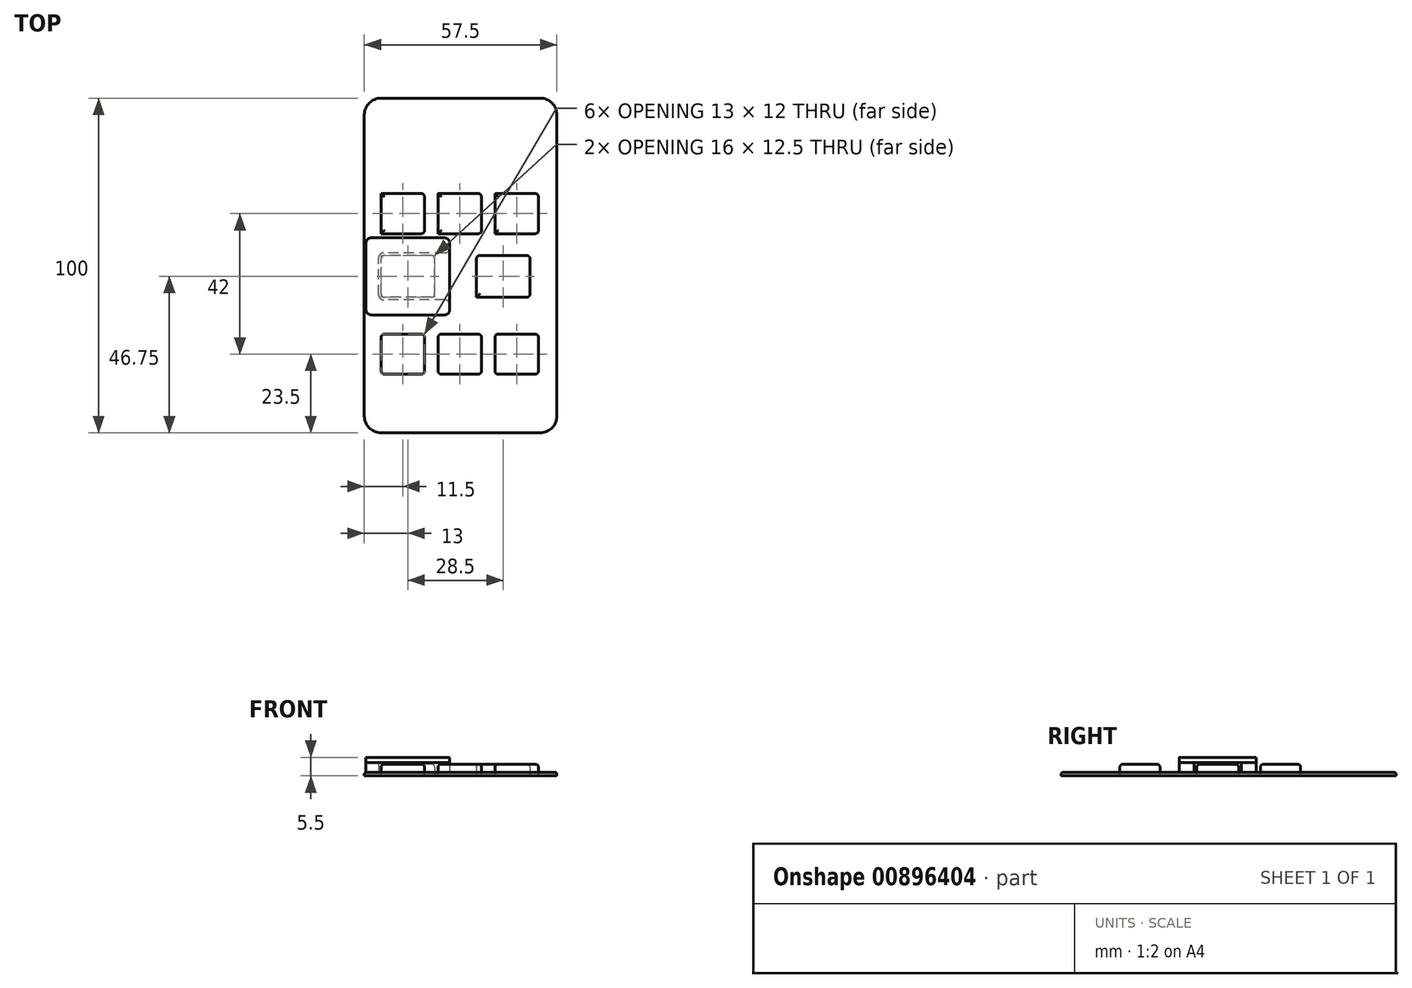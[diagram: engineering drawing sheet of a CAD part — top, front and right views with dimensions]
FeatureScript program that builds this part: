
annotation { "Feature Type Name" : "Feature", "Feature Type Description" : "" }
export const myFeature = defineFeature(function(context is Context, id is Id, definition is map)
    precondition{}
    {
        {
            var Q0;
            Q0=qCreatedBy(makeId("Top.planeOp"),FACE);
            var sketch = newSketch(context, id + "F0", { "sketchPlane" : qUnion([Q0])});
            skLineSegment(sketch, "E0.bottom", {"start": v(28.75, -50) * mm, "end": v(-28.75, -50) * mm});
            skLineSegment(sketch, "E0.top", {"start": v(28.75, 50) * mm, "end": v(-28.75, 50) * mm});
            skLineSegment(sketch, "E0.left", {"start": v(28.75, -50) * mm, "end": v(28.75, 50) * mm});
            skLineSegment(sketch, "E0.right", {"start": v(-28.75, -50) * mm, "end": v(-28.75, 50) * mm});
            skPoint(sketch, "E0.middle", {"position": v(0, 0) * mm});
            skSolve(sketch);
        }
        {
            var Q0;
            Q0=makeQuery(id+"F0.imprint","IMPRINT",FACE,{"disambiguationData":[TD([[makeQuery(id+"F0.imprint","IMPRINT",EDGE,{"derivedFrom":sQuery(id+"F0.wireOp",EDGE,"E0.bottom")}),-1.0]])]});
            extrude(context, id + "F1", {"entities" : qUnion([Q0]), "depth" : 1 * mm, "offsetDistance" : 25 * mm});
        }
        {
            var Q0;
            Q0=makeQuery(id+"F1.opExtrude","CAP_FACE",FACE,{"disambiguationData":[OSD([sQuery(id+"F0.wireOp",EDGE,"E0.bottom"),sQuery(id+"F0.wireOp",EDGE,"E0.top"),sQuery(id+"F0.wireOp",EDGE,"E0.left"),sQuery(id+"F0.wireOp",EDGE,"E0.right")])],"isStart":false});
            var sketch = newSketch(context, id + "F2", { "sketchPlane" : qUnion([Q0])});
            skPoint(sketch, "E1.middle", {"position": v(0, 0) * mm});
            skLineSegment(sketch, "E2.bottom", {"start": v(-7.75, -9.5) * mm, "end": v(-23.75, -9.5) * mm});
            skLineSegment(sketch, "E2.top", {"start": v(-8.75, 3) * mm, "end": v(-22.75, 3) * mm});
            skLineSegment(sketch, "E2.left", {"start": v(-7.75, -8.5) * mm, "end": v(-7.75, 2) * mm});
            skLineSegment(sketch, "E2.right", {"start": v(-23.75, -8.5) * mm, "end": v(-23.75, 2) * mm});
            skPoint(sketch, "E2.middle", {"position": v(-15.75, -3.25) * mm});
            skLineSegment(sketch, "E3.bottom", {"start": v(-11.75, 9.5) * mm, "end": v(-24, 9.5) * mm});
            skLineSegment(sketch, "E3.top", {"start": v(-11.75, 21.5) * mm, "end": v(-24, 21.5) * mm});
            skLineSegment(sketch, "E3.left", {"start": v(-10.75, 10.5) * mm, "end": v(-10.75, 20.5) * mm});
            skLineSegment(sketch, "E3.right", {"start": v(-23.75, 9.5) * mm, "end": v(-23.75, 21.5) * mm});
            skPoint(sketch, "E3.middle", {"position": v(-17.25, 15.5) * mm});
            skLineSegment(sketch, "E4.bottom", {"start": v(-10.75, -32.5) * mm, "end": v(-23.75, -32.5) * mm});
            skLineSegment(sketch, "E4.top", {"start": v(-11.75, -20.5) * mm, "end": v(-22.75, -20.5) * mm});
            skLineSegment(sketch, "E4.left", {"start": v(-10.75, -31.5) * mm, "end": v(-10.75, -21.5) * mm});
            skLineSegment(sketch, "E4.right", {"start": v(-23.75, -31.5) * mm, "end": v(-23.75, -21.5) * mm});
            skPoint(sketch, "E4.middle", {"position": v(-17.25, -26.5) * mm});
            skPoint(sketch, "E5.1.0.0", {"position": v(-0.25, 15.5) * mm});
            skLineSegment(sketch, "E5.1.0.1", {"start": v(-8, 10.5) * mm, "end": v(-8, 20.5) * mm, "construction": true});
            skLineSegment(sketch, "E5.1.0.2", {"start": v(6.25, 10.5) * mm, "end": v(6.25, 20.5) * mm});
            skLineSegment(sketch, "E5.1.0.3", {"start": v(5.25, 21.5) * mm, "end": v(-7, 21.5) * mm});
            skLineSegment(sketch, "E5.1.0.4", {"start": v(5.25, 9.5) * mm, "end": v(-7, 9.5) * mm});
            skLineSegment(sketch, "E5.1.0.5", {"start": v(-6.75, 9.5) * mm, "end": v(-6.75, 21.5) * mm});
            skPoint(sketch, "E5.2.0.0", {"position": v(16.75, 15.5) * mm});
            skLineSegment(sketch, "E5.2.0.1", {"start": v(9, 10.5) * mm, "end": v(9, 20.5) * mm, "construction": true});
            skLineSegment(sketch, "E5.2.0.2", {"start": v(23.25, 10.5) * mm, "end": v(23.25, 20.5) * mm});
            skLineSegment(sketch, "E5.2.0.3", {"start": v(22.25, 21.5) * mm, "end": v(10, 21.5) * mm});
            skLineSegment(sketch, "E5.2.0.4", {"start": v(22.25, 9.5) * mm, "end": v(10, 9.5) * mm});
            skLineSegment(sketch, "E5.2.0.5", {"start": v(10.25, 9.5) * mm, "end": v(10.25, 21.5) * mm});
            skLineSegment(sketch, "E5.direction1", {"start": v(-25, -37.5) * mm, "end": v(-8, -37.5) * mm, "construction": true});
            skLineSegment(sketch, "E6.1.0.0", {"start": v(-6.75, -31.5) * mm, "end": v(-6.75, -21.5) * mm});
            skLineSegment(sketch, "E6.1.0.1", {"start": v(6.25, -31.5) * mm, "end": v(6.25, -21.5) * mm});
            skLineSegment(sketch, "E6.1.0.2", {"start": v(5.25, -32.5) * mm, "end": v(-5.75, -32.5) * mm});
            skLineSegment(sketch, "E6.1.0.3", {"start": v(5.25, -20.5) * mm, "end": v(-5.75, -20.5) * mm});
            skPoint(sketch, "E6.1.0.4", {"position": v(-0.25, -26.5) * mm});
            skLineSegment(sketch, "E6.2.0.0", {"start": v(10.25, -31.5) * mm, "end": v(10.25, -21.5) * mm});
            skLineSegment(sketch, "E6.2.0.1", {"start": v(23.25, -31.5) * mm, "end": v(23.25, -21.5) * mm});
            skLineSegment(sketch, "E6.2.0.2", {"start": v(22.25, -32.5) * mm, "end": v(11.25, -32.5) * mm});
            skLineSegment(sketch, "E6.2.0.3", {"start": v(22.25, -20.5) * mm, "end": v(11.25, -20.5) * mm});
            skPoint(sketch, "E6.2.0.4", {"position": v(16.75, -26.5) * mm});
            skLineSegment(sketch, "E6.direction1", {"start": v(-22.75, -32.5) * mm, "end": v(-11.75, -32.5) * mm, "construction": true});
            skLineSegment(sketch, "E7.1.0.0", {"start": v(4.75, -9.5) * mm, "end": v(4.75, 2) * mm});
            skPoint(sketch, "E7.1.0.1", {"position": v(12.75, -3.25) * mm});
            skLineSegment(sketch, "E7.1.0.2", {"start": v(20.75, -8.5) * mm, "end": v(20.75, 2) * mm});
            skPoint(sketch, "E7.1.0.3", {"position": v(28.5, 0) * mm});
            skLineSegment(sketch, "E7.1.0.4", {"start": v(19.75, -9.5) * mm, "end": v(4.75, -9.5) * mm});
            skLineSegment(sketch, "E7.1.0.5", {"start": v(19.75, 3) * mm, "end": v(5.75, 3) * mm});
            skLineSegment(sketch, "E7.direction1", {"start": v(-22.75, -9.5) * mm, "end": v(-8.75, -9.5) * mm, "construction": true});
            skPoint(sketch, "E8.newPointA", {"position": v(-23.75, 21.5) * mm});
            skPoint(sketch, "E8.newPointB", {"position": v(-25, 37.5) * mm});
            skArc(sketch, "E8.filletArc", {"start": v(-24, 21.5) * mm, "mid": v(-24.7, 21.2) * mm, "end": v(-25, 20.5) * mm});
            skPoint(sketch, "E9.visualSharp", {"position": v(-10.75, 21.5) * mm});
            skArc(sketch, "E9.filletArc", {"start": v(-10.75, 20.5) * mm, "mid": v(-11.04, 21.2) * mm, "end": v(-11.75, 21.5) * mm});
            skPoint(sketch, "E10.visualSharp", {"position": v(-10.75, 9.5) * mm});
            skArc(sketch, "E10.filletArc", {"start": v(-11.75, 9.5) * mm, "mid": v(-11.04, 9.8) * mm, "end": v(-10.75, 10.5) * mm});
            skPoint(sketch, "E11.newPointA", {"position": v(-25, -37.5) * mm});
            skPoint(sketch, "E11.newPointB", {"position": v(-23.75, 9.5) * mm});
            skArc(sketch, "E11.filletArc", {"start": v(-25, 10.5) * mm, "mid": v(-24.7, 9.8) * mm, "end": v(-24, 9.5) * mm});
            skPoint(sketch, "E12.newPointA", {"position": v(-6.75, 21.5) * mm});
            skPoint(sketch, "E12.newPointB", {"position": v(-8, 37.5) * mm});
            skArc(sketch, "E12.filletArc", {"start": v(-7, 21.5) * mm, "mid": v(-7.7, 21.2) * mm, "end": v(-8, 20.5) * mm});
            skPoint(sketch, "E13.newPointA", {"position": v(-6.75, 9.5) * mm});
            skPoint(sketch, "E13.newPointB", {"position": v(-8, -37.5) * mm});
            skArc(sketch, "E13.filletArc", {"start": v(-8, 10.5) * mm, "mid": v(-7.7, 9.8) * mm, "end": v(-7, 9.5) * mm});
            skPoint(sketch, "E14.visualSharp", {"position": v(6.25, 9.5) * mm});
            skArc(sketch, "E14.filletArc", {"start": v(5.25, 9.5) * mm, "mid": v(5.96, 9.8) * mm, "end": v(6.25, 10.5) * mm});
            skPoint(sketch, "E15.visualSharp", {"position": v(6.25, 21.5) * mm});
            skArc(sketch, "E15.filletArc", {"start": v(6.25, 20.5) * mm, "mid": v(5.96, 21.2) * mm, "end": v(5.25, 21.5) * mm});
            skPoint(sketch, "E16.newPointA", {"position": v(10.25, 21.5) * mm});
            skPoint(sketch, "E16.newPointB", {"position": v(9, 37.5) * mm});
            skArc(sketch, "E16.filletArc", {"start": v(10, 21.5) * mm, "mid": v(9.3, 21.2) * mm, "end": v(9, 20.5) * mm});
            skPoint(sketch, "E17.newPointA", {"position": v(10.25, 9.5) * mm});
            skPoint(sketch, "E17.newPointB", {"position": v(9, -37.5) * mm});
            skArc(sketch, "E17.filletArc", {"start": v(9, 10.5) * mm, "mid": v(9.3, 9.8) * mm, "end": v(10, 9.5) * mm});
            skPoint(sketch, "E18.visualSharp", {"position": v(23.25, 9.5) * mm});
            skArc(sketch, "E18.filletArc", {"start": v(22.25, 9.5) * mm, "mid": v(22.96, 9.8) * mm, "end": v(23.25, 10.5) * mm});
            skPoint(sketch, "E19.visualSharp", {"position": v(23.25, 21.5) * mm});
            skArc(sketch, "E19.filletArc", {"start": v(23.25, 20.5) * mm, "mid": v(22.96, 21.2) * mm, "end": v(22.25, 21.5) * mm});
            skPoint(sketch, "E20.visualSharp", {"position": v(20.75, 3) * mm});
            skArc(sketch, "E20.filletArc", {"start": v(20.75, 2) * mm, "mid": v(20.46, 2.7) * mm, "end": v(19.75, 3) * mm});
            skPoint(sketch, "E21.visualSharp", {"position": v(20.75, -9.5) * mm});
            skArc(sketch, "E21.filletArc", {"start": v(19.75, -9.5) * mm, "mid": v(20.46, -9.2) * mm, "end": v(20.75, -8.5) * mm});
            skPoint(sketch, "E22.visualSharp", {"position": v(4.75, 3) * mm});
            skArc(sketch, "E22.filletArc", {"start": v(5.75, 3) * mm, "mid": v(5.04, 2.7) * mm, "end": v(4.75, 2) * mm});
            skPoint(sketch, "E23.newPointA", {"position": v(4.75, -9.5) * mm});
            skPoint(sketch, "E23.newPointB", {"position": v(-7.75, -9.5) * mm});
            skArc(sketch, "E23.filletArc", {"start": v(-8.75, -9.5) * mm, "mid": v(-8.04, -9.2) * mm, "end": v(-7.75, -8.5) * mm});
            skPoint(sketch, "E24.visualSharp", {"position": v(-23.75, 3) * mm});
            skArc(sketch, "E24.filletArc", {"start": v(-22.75, 3) * mm, "mid": v(-23.46, 2.7) * mm, "end": v(-23.75, 2) * mm});
            skPoint(sketch, "E25.visualSharp", {"position": v(-7.75, 3) * mm});
            skArc(sketch, "E25.filletArc", {"start": v(-7.75, 2) * mm, "mid": v(-8.04, 2.7) * mm, "end": v(-8.75, 3) * mm});
            skPoint(sketch, "E26.visualSharp", {"position": v(-23.75, -9.5) * mm});
            skArc(sketch, "E26.filletArc", {"start": v(-23.75, -8.5) * mm, "mid": v(-23.46, -9.2) * mm, "end": v(-22.75, -9.5) * mm});
            skPoint(sketch, "E27.visualSharp", {"position": v(-23.75, -20.5) * mm});
            skArc(sketch, "E27.filletArc", {"start": v(-22.75, -20.5) * mm, "mid": v(-23.46, -20.8) * mm, "end": v(-23.75, -21.5) * mm});
            skPoint(sketch, "E28.visualSharp", {"position": v(-23.75, -32.5) * mm});
            skArc(sketch, "E28.filletArc", {"start": v(-23.75, -31.5) * mm, "mid": v(-23.46, -32.2) * mm, "end": v(-22.75, -32.5) * mm});
            skPoint(sketch, "E29.newPointA", {"position": v(-6.75, -32.5) * mm});
            skPoint(sketch, "E29.newPointB", {"position": v(-10.75, -32.5) * mm});
            skArc(sketch, "E29.filletArc", {"start": v(-11.75, -32.5) * mm, "mid": v(-11.04, -32.2) * mm, "end": v(-10.75, -31.5) * mm});
            skPoint(sketch, "E30.visualSharp", {"position": v(-10.75, -20.5) * mm});
            skArc(sketch, "E30.filletArc", {"start": v(-10.75, -21.5) * mm, "mid": v(-11.04, -20.8) * mm, "end": v(-11.75, -20.5) * mm});
            skPoint(sketch, "E31.visualSharp", {"position": v(-6.75, -20.5) * mm});
            skArc(sketch, "E31.filletArc", {"start": v(-5.75, -20.5) * mm, "mid": v(-6.46, -20.8) * mm, "end": v(-6.75, -21.5) * mm});
            skArc(sketch, "E32.filletArc", {"start": v(-6.75, -31.5) * mm, "mid": v(-6.46, -32.2) * mm, "end": v(-5.75, -32.5) * mm});
            skPoint(sketch, "E33.visualSharp", {"position": v(6.25, -32.5) * mm});
            skArc(sketch, "E33.filletArc", {"start": v(5.25, -32.5) * mm, "mid": v(5.96, -32.2) * mm, "end": v(6.25, -31.5) * mm});
            skPoint(sketch, "E34.visualSharp", {"position": v(6.25, -20.5) * mm});
            skArc(sketch, "E34.filletArc", {"start": v(6.25, -21.5) * mm, "mid": v(5.96, -20.8) * mm, "end": v(5.25, -20.5) * mm});
            skPoint(sketch, "E35.visualSharp", {"position": v(10.25, -20.5) * mm});
            skArc(sketch, "E35.filletArc", {"start": v(11.25, -20.5) * mm, "mid": v(10.54, -20.8) * mm, "end": v(10.25, -21.5) * mm});
            skPoint(sketch, "E36.visualSharp", {"position": v(10.25, -32.5) * mm});
            skArc(sketch, "E36.filletArc", {"start": v(10.25, -31.5) * mm, "mid": v(10.54, -32.2) * mm, "end": v(11.25, -32.5) * mm});
            skPoint(sketch, "E37.visualSharp", {"position": v(23.25, -32.5) * mm});
            skArc(sketch, "E37.filletArc", {"start": v(22.25, -32.5) * mm, "mid": v(22.96, -32.2) * mm, "end": v(23.25, -31.5) * mm});
            skPoint(sketch, "E38.visualSharp", {"position": v(23.25, -20.5) * mm});
            skArc(sketch, "E38.filletArc", {"start": v(23.25, -21.5) * mm, "mid": v(22.96, -20.8) * mm, "end": v(22.25, -20.5) * mm});
            skSolve(sketch);
        }
        {
            var Q0;
            Q0 = qSketchRegion(id + "F2", true);
            extrude(context, id + "F3", {"entities" : qUnion([Q0]), "depth" : 2.5 * mm, "offsetDistance" : 25 * mm});
        }
        {
            var Q0;
            Q0=makeQuery(id+"F3.opExtrude","CAP_FACE",FACE,{"disambiguationData":[OSD([sQuery(id+"F2.wireOp",EDGE,"E3.bottom"),sQuery(id+"F2.wireOp",EDGE,"E3.top"),sQuery(id+"F2.wireOp",EDGE,"E3.left"),sQuery(id+"F2.wireOp",EDGE,"E3.right"),sQuery(id+"F2.wireOp",EDGE,"E8.filletArc"),sQuery(id+"F2.wireOp",EDGE,"E9.filletArc"),sQuery(id+"F2.wireOp",EDGE,"E10.filletArc"),sQuery(id+"F2.wireOp",EDGE,"E11.filletArc")])],"isStart":false});
            var Q1;
            Q1=makeQuery(id+"F3.opExtrude","CAP_FACE",FACE,{"disambiguationData":[OSD([sQuery(id+"F2.wireOp",EDGE,"E5.1.0.2"),sQuery(id+"F2.wireOp",EDGE,"E5.1.0.3"),sQuery(id+"F2.wireOp",EDGE,"E5.1.0.4"),sQuery(id+"F2.wireOp",EDGE,"E5.1.0.5"),sQuery(id+"F2.wireOp",EDGE,"E12.filletArc"),sQuery(id+"F2.wireOp",EDGE,"E13.filletArc"),sQuery(id+"F2.wireOp",EDGE,"E14.filletArc"),sQuery(id+"F2.wireOp",EDGE,"E15.filletArc")])],"isStart":false});
            var Q2;
            Q2=makeQuery(id+"F3.opExtrude","CAP_FACE",FACE,{"disambiguationData":[OSD([sQuery(id+"F2.wireOp",EDGE,"E5.2.0.2"),sQuery(id+"F2.wireOp",EDGE,"E5.2.0.3"),sQuery(id+"F2.wireOp",EDGE,"E5.2.0.4"),sQuery(id+"F2.wireOp",EDGE,"E5.2.0.5"),sQuery(id+"F2.wireOp",EDGE,"E16.filletArc"),sQuery(id+"F2.wireOp",EDGE,"E17.filletArc"),sQuery(id+"F2.wireOp",EDGE,"E18.filletArc"),sQuery(id+"F2.wireOp",EDGE,"E19.filletArc")])],"isStart":false});
            var Q3;
            Q3=makeQuery(id+"F3.opExtrude","CAP_FACE",FACE,{"disambiguationData":[OSD([sQuery(id+"F2.wireOp",EDGE,"E2.bottom"),sQuery(id+"F2.wireOp",EDGE,"E2.top"),sQuery(id+"F2.wireOp",EDGE,"E2.left"),sQuery(id+"F2.wireOp",EDGE,"E2.right"),sQuery(id+"F2.wireOp",EDGE,"E23.filletArc"),sQuery(id+"F2.wireOp",EDGE,"E24.filletArc"),sQuery(id+"F2.wireOp",EDGE,"E25.filletArc"),sQuery(id+"F2.wireOp",EDGE,"E26.filletArc")])],"isStart":false});
            var Q4;
            Q4=makeQuery(id+"F3.opExtrude","CAP_FACE",FACE,{"disambiguationData":[OSD([sQuery(id+"F2.wireOp",EDGE,"E7.1.0.0"),sQuery(id+"F2.wireOp",EDGE,"E7.1.0.2"),sQuery(id+"F2.wireOp",EDGE,"E7.1.0.4"),sQuery(id+"F2.wireOp",EDGE,"E7.1.0.5"),sQuery(id+"F2.wireOp",EDGE,"E20.filletArc"),sQuery(id+"F2.wireOp",EDGE,"E21.filletArc"),sQuery(id+"F2.wireOp",EDGE,"E22.filletArc")])],"isStart":false});
            var Q5;
            Q5=makeQuery(id+"F3.opExtrude","CAP_FACE",FACE,{"disambiguationData":[OSD([sQuery(id+"F2.wireOp",EDGE,"E6.2.0.0"),sQuery(id+"F2.wireOp",EDGE,"E6.2.0.1"),sQuery(id+"F2.wireOp",EDGE,"E6.2.0.2"),sQuery(id+"F2.wireOp",EDGE,"E6.2.0.3"),sQuery(id+"F2.wireOp",EDGE,"E35.filletArc"),sQuery(id+"F2.wireOp",EDGE,"E36.filletArc"),sQuery(id+"F2.wireOp",EDGE,"E37.filletArc"),sQuery(id+"F2.wireOp",EDGE,"E38.filletArc")])],"isStart":false});
            var Q6;
            Q6=makeQuery(id+"F3.opExtrude","CAP_FACE",FACE,{"disambiguationData":[OSD([sQuery(id+"F2.wireOp",EDGE,"E6.1.0.0"),sQuery(id+"F2.wireOp",EDGE,"E6.1.0.1"),sQuery(id+"F2.wireOp",EDGE,"E6.1.0.2"),sQuery(id+"F2.wireOp",EDGE,"E6.1.0.3"),sQuery(id+"F2.wireOp",EDGE,"E31.filletArc"),sQuery(id+"F2.wireOp",EDGE,"E32.filletArc"),sQuery(id+"F2.wireOp",EDGE,"E33.filletArc"),sQuery(id+"F2.wireOp",EDGE,"E34.filletArc")])],"isStart":false});
            var Q7;
            Q7=makeQuery(id+"F3.opExtrude","CAP_FACE",FACE,{"disambiguationData":[OSD([sQuery(id+"F2.wireOp",EDGE,"E4.bottom"),sQuery(id+"F2.wireOp",EDGE,"E4.top"),sQuery(id+"F2.wireOp",EDGE,"E4.left"),sQuery(id+"F2.wireOp",EDGE,"E4.right"),sQuery(id+"F2.wireOp",EDGE,"E27.filletArc"),sQuery(id+"F2.wireOp",EDGE,"E28.filletArc"),sQuery(id+"F2.wireOp",EDGE,"E29.filletArc"),sQuery(id+"F2.wireOp",EDGE,"E30.filletArc")])],"isStart":false});
            fillet(context, id + "F4", {"entities" : qUnion([Q0, Q1, Q2, Q3, Q4, Q5, Q6, Q7]), "radius" : 1 * mm, "tangentPropagation" : true, "allowEdgeOverflow" : false});
        }
        {
            var Q0;
            Q0=makeQuery(id+"F1.opExtrude","SWEPT_EDGE",EDGE,{"disambiguationData":[OSD([sQuery(id+"F0.wireOp",EDGE,"E0.top"),sQuery(id+"F0.wireOp",EDGE,"E0.right")])]});
            var Q1;
            Q1=makeQuery(id+"F1.opExtrude","SWEPT_EDGE",EDGE,{"disambiguationData":[OSD([sQuery(id+"F0.wireOp",EDGE,"E0.top"),sQuery(id+"F0.wireOp",EDGE,"E0.left")])]});
            var Q2;
            Q2=makeQuery(id+"F1.opExtrude","SWEPT_EDGE",EDGE,{"disambiguationData":[OSD([sQuery(id+"F0.wireOp",EDGE,"E0.bottom"),sQuery(id+"F0.wireOp",EDGE,"E0.left")])]});
            var Q3;
            Q3=makeQuery(id+"F1.opExtrude","SWEPT_EDGE",EDGE,{"disambiguationData":[OSD([sQuery(id+"F0.wireOp",EDGE,"E0.bottom"),sQuery(id+"F0.wireOp",EDGE,"E0.right")])]});
            fillet(context, id + "F5", {"entities" : qUnion([Q0, Q1, Q2, Q3]), "radius" : 5 * mm, "tangentPropagation" : true, "allowEdgeOverflow" : false});
        }
        {
            var Q0;
            Q0=makeQuery(id+"F1.opExtrude","CAP_FACE",FACE,{"disambiguationData":[OSD([sQuery(id+"F0.wireOp",EDGE,"E0.bottom"),sQuery(id+"F0.wireOp",EDGE,"E0.top"),sQuery(id+"F0.wireOp",EDGE,"E0.left"),sQuery(id+"F0.wireOp",EDGE,"E0.right")])],"isStart":false});
            fillet(context, id + "F6", {"entities" : qUnion([Q0]), "radius" : .5 * mm, "tangentPropagation" : true, "allowEdgeOverflow" : false});
        }
        {
            var Q0;
            Q0 = qSketchRegion(id + "F2", true);
            extrude(context, id + "F7", {"entities" : qUnion([Q0]), "operationType" : NewBodyOperationType.REMOVE, "oppositeDirection" : true, "depth" : 25 * mm, "offsetDistance" : 25 * mm});
        }
        {
            var Q0;
            Q0=makeQuery(id+"F1.opExtrude","CAP_FACE",FACE,{"disambiguationData":[OSD([sQuery(id+"F0.wireOp",EDGE,"E0.bottom"),sQuery(id+"F0.wireOp",EDGE,"E0.top"),sQuery(id+"F0.wireOp",EDGE,"E0.left"),sQuery(id+"F0.wireOp",EDGE,"E0.right")])],"isStart":false});
            var sketch = newSketch(context, id + "F8", { "sketchPlane" : qUnion([Q0])});
            skLineSegment(sketch, "E39", {"start": v(-23.75, -3.25) * mm, "end": v(-7.75, -3.25) * mm, "construction": true});
            skLineSegment(sketch, "E40", {"start": v(-15.75, 3) * mm, "end": v(-15.75, -9.5) * mm, "construction": true});
            skLineSegment(sketch, "E41.bottom", {"start": v(-4.75, -10.25) * mm, "end": v(-23, -10.25) * mm});
            skLineSegment(sketch, "E41.top", {"start": v(-4.75, 3.75) * mm, "end": v(-23, 3.75) * mm});
            skLineSegment(sketch, "E41.right", {"start": v(-24.5, -8.75) * mm, "end": v(-24.5, 2.25) * mm});
            skPoint(sketch, "E41.middle", {"position": v(-15.75, -3.25) * mm});
            skLineSegment(sketch, "E42.bottom", {"start": v(-26.75, -14.75) * mm, "end": v(-4.75, -14.75) * mm});
            skLineSegment(sketch, "E42.top", {"start": v(-26.75, 8.25) * mm, "end": v(-4.85, 8.25) * mm});
            skLineSegment(sketch, "E42.left", {"start": v(-28.25, -13.25) * mm, "end": v(-28.25, 6.75) * mm});
            skLineSegment(sketch, "E42.right", {"start": v(-3.25, -13.25) * mm, "end": v(-3.25, -11.75) * mm});
            skPoint(sketch, "E41.left.end.orphan", {"position": v(-7, 3.75) * mm});
            skPoint(sketch, "E41.left.start.orphan", {"position": v(-7, -10.25) * mm});
            skLineSegment(sketch, "E43.trimOffspring", {"start": v(-3.25, 5.25) * mm, "end": v(-3.25, 6.65) * mm});
            skPoint(sketch, "E44.visualSharp", {"position": v(-28.25, 8.25) * mm});
            skArc(sketch, "E44.filletArc", {"start": v(-26.75, 8.25) * mm, "mid": v(-27.81, 7.81) * mm, "end": v(-28.25, 6.75) * mm});
            skPoint(sketch, "E45.visualSharp", {"position": v(-3.25, 8.25) * mm});
            skArc(sketch, "E45.filletArc", {"start": v(-3.25, 6.65) * mm, "mid": v(-3.72, 7.78) * mm, "end": v(-4.85, 8.25) * mm});
            skPoint(sketch, "E46.visualSharp", {"position": v(-3.25, 3.75) * mm});
            skArc(sketch, "E46.filletArc", {"start": v(-4.75, 3.75) * mm, "mid": v(-3.69, 4.19) * mm, "end": v(-3.25, 5.25) * mm});
            skPoint(sketch, "E47.visualSharp", {"position": v(-24.5, 3.75) * mm});
            skArc(sketch, "E47.filletArc", {"start": v(-23, 3.75) * mm, "mid": v(-24.06, 3.31) * mm, "end": v(-24.5, 2.25) * mm});
            skPoint(sketch, "E48.visualSharp", {"position": v(-24.5, -10.25) * mm});
            skArc(sketch, "E48.filletArc", {"start": v(-24.5, -8.75) * mm, "mid": v(-24.06, -9.81) * mm, "end": v(-23, -10.25) * mm});
            skPoint(sketch, "E49.visualSharp", {"position": v(-3.25, -10.25) * mm});
            skArc(sketch, "E49.filletArc", {"start": v(-3.25, -11.75) * mm, "mid": v(-3.69, -10.69) * mm, "end": v(-4.75, -10.25) * mm});
            skPoint(sketch, "E50.visualSharp", {"position": v(-3.25, -14.75) * mm});
            skArc(sketch, "E50.filletArc", {"start": v(-4.75, -14.75) * mm, "mid": v(-3.69, -14.31) * mm, "end": v(-3.25, -13.25) * mm});
            skPoint(sketch, "E51.visualSharp", {"position": v(-28.25, -14.75) * mm});
            skArc(sketch, "E51.filletArc", {"start": v(-28.25, -13.25) * mm, "mid": v(-27.81, -14.31) * mm, "end": v(-26.75, -14.75) * mm});
            skSolve(sketch);
        }
        {
            var Q0;
            Q0 = qSketchRegion(id + "F8", true);
            extrude(context, id + "F9", {"entities" : qUnion([Q0]), "depth" : 3 * mm, "offsetDistance" : 25 * mm});
        }
        {
            var Q0;
            Q0=makeQuery(id+"F9.opExtrude","CAP_FACE",FACE,{"disambiguationData":[OSD([sQuery(id+"F8.wireOp",EDGE,"E41.bottom"),sQuery(id+"F8.wireOp",EDGE,"E41.top"),sQuery(id+"F8.wireOp",EDGE,"E41.right"),sQuery(id+"F8.wireOp",EDGE,"E42.bottom"),sQuery(id+"F8.wireOp",EDGE,"E42.top"),sQuery(id+"F8.wireOp",EDGE,"E42.left"),sQuery(id+"F8.wireOp",EDGE,"E42.right"),sQuery(id+"F8.wireOp",EDGE,"E43.trimOffspring"),sQuery(id+"F8.wireOp",EDGE,"E44.filletArc"),sQuery(id+"F8.wireOp",EDGE,"E45.filletArc"),sQuery(id+"F8.wireOp",EDGE,"E46.filletArc"),sQuery(id+"F8.wireOp",EDGE,"E47.filletArc"),sQuery(id+"F8.wireOp",EDGE,"E48.filletArc"),sQuery(id+"F8.wireOp",EDGE,"E49.filletArc"),sQuery(id+"F8.wireOp",EDGE,"E50.filletArc"),sQuery(id+"F8.wireOp",EDGE,"E51.filletArc")])],"isStart":false});
            var sketch = newSketch(context, id + "F10", { "sketchPlane" : qUnion([Q0])});
            skLineSegment(sketch, "E52.0.0", {"start": v(-4.85, 8.25) * mm, "end": v(-26.75, 8.25) * mm});
            skArc(sketch, "E52.0.1", {"start": v(-26.75, 8.25) * mm, "mid": v(-27.81, 7.81) * mm, "end": v(-28.25, 6.75) * mm});
            skLineSegment(sketch, "E52.0.2", {"start": v(-28.25, 6.75) * mm, "end": v(-28.25, -13.25) * mm});
            skArc(sketch, "E52.0.3", {"start": v(-28.25, -13.25) * mm, "mid": v(-27.81, -14.31) * mm, "end": v(-26.75, -14.75) * mm});
            skLineSegment(sketch, "E52.0.4", {"start": v(-26.75, -14.75) * mm, "end": v(-4.75, -14.75) * mm});
            skArc(sketch, "E52.0.5", {"start": v(-4.75, -14.75) * mm, "mid": v(-3.69, -14.31) * mm, "end": v(-3.25, -13.25) * mm});
            skArc(sketch, "E52.0.15", {"start": v(-3.25, 6.65) * mm, "mid": v(-3.72, 7.78) * mm, "end": v(-4.85, 8.25) * mm});
            skLineSegment(sketch, "E53", {"start": v(-3.25, 6.65) * mm, "end": v(-3.25, -13.25) * mm});
            skSolve(sketch);
        }
        {
            var Q0;
            Q0 = qSketchRegion(id + "F10", true);
            extrude(context, id + "F11", {"entities" : qUnion([Q0]), "depth" : 1.5 * mm, "offsetDistance" : 25 * mm});
        }
    });
